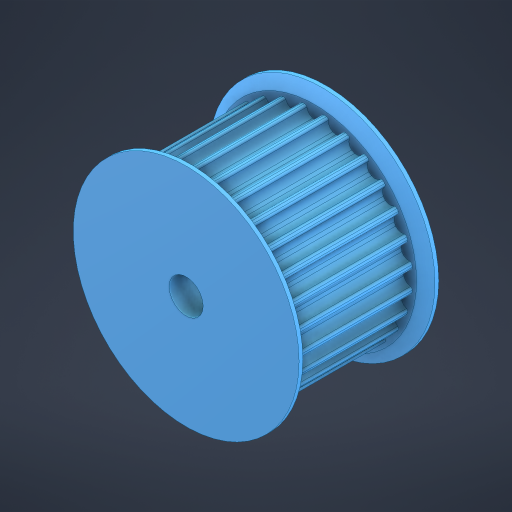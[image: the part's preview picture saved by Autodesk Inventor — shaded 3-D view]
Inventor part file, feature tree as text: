
AUTODESK INVENTOR PART (.ipt)
format: ipt  version: 2024.2 (Build 282272000, 272)  size: 512,512 bytes
history: native  units: in
note: dims shown in document units (in); Inventor stores cm internally (conversion verified against a paired STEP export)
features: other x2, extrude x1, sketch x1
ambient origin geometry x8: Origin, YZ Plane, XZ Plane, XY Plane, X Axis, Y Axis, Z Axis, Center Point
bodies: Solid1 (feature_tree)
feature tree (4):
  other  "HTD Pulley - 28 Tooth.step"
  extrude  "Extrusion1"  Depth=0.5207in TaperAngle=0.0deg
  sketch  "Sketch1"  dims[d0=0.3937in d1=0.5207in d2=0.0in]
  other  "Part 1"
